# Revit family: 687469SS CARE SUPPORT 140DEG 1110X940X700 RH
name_source: partatom
category: Plumbing Fixtures
units: mm (PartAtom-declared; Revit-internal decimal feet)

## family parameters
Cut with Voids When Loaded = No
Host = Face
OmniClass Number = 23.40.20.21.47
OmniClass Title = Bath Grab Bars
Part Type = Normal
Room Calculation Point = No
Round Connector Dimension = Use Radius
Shared = No

## types (1)
- CARE SUPPORT 140DEG 1110X940X700 RH
    Assembly Code = C1030200
    CW Connection = No
    Default Elevation = 0 mm  [stored 0 ft]
    Description = CARE SUPPORT 140DEG 1110X940X700 RH
    HW Connection = No
    Manufacturer = GWA Bathrooms & Kitchens
    Material_Base = GWA_Metal-Stainless
    Model = 687469SS
    Rail_Height = 73 mm  [stored 0.239501 ft]
    Rail_Width = 700 mm  [stored 2.29659 ft]
    URL = https://www.caroma.com.au
    Vent Connection = No
    Waste Connection = No

note: [stored X ft] marks values corroborated as IEEE doubles in the binary element streams (Revit-internal decimal feet)

## geometry (parser evidence)
native form markers: Sweep x2
no freeform markers — native parametric forms only
